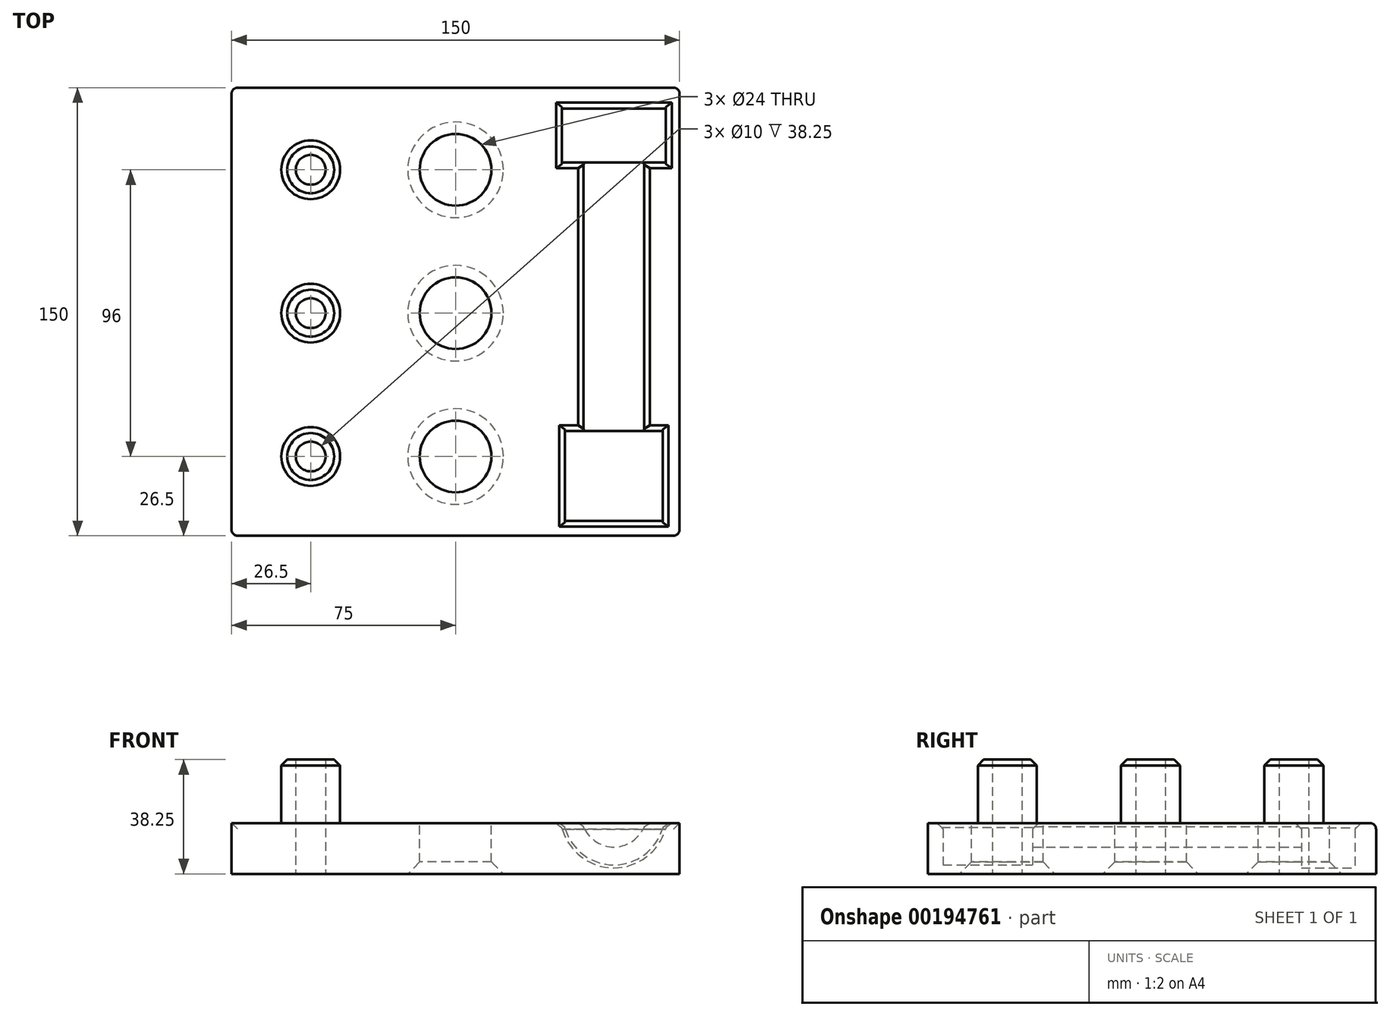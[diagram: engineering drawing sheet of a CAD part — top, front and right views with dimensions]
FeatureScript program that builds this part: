
annotation { "Feature Type Name" : "Feature", "Feature Type Description" : "" }
export const myFeature = defineFeature(function(context is Context, id is Id, definition is map)
    precondition{}
    {
        {
            var Q0;
            Q0=qCreatedBy(makeId("Top.planeOp"),FACE);
            var sketch = newSketch(context, id + "F0", { "sketchPlane" : qUnion([Q0])});
            skLineSegment(sketch, "E0.bottom", {"start": v(0, 0) * mm, "end": v(150, 0) * mm});
            skLineSegment(sketch, "E0.top", {"start": v(0, 150) * mm, "end": v(150, 150) * mm});
            skLineSegment(sketch, "E0.left", {"start": v(0, 0) * mm, "end": v(0, 150) * mm});
            skLineSegment(sketch, "E0.right", {"start": v(150, 0) * mm, "end": v(150, 150) * mm});
            skSolve(sketch);
        }
        {
            var Q0;
            Q0=makeQuery(id+"F0.imprint","IMPRINT",FACE,{"disambiguationData":[TD([[makeQuery(id+"F0.imprint","IMPRINT",EDGE,{"derivedFrom":sQuery(id+"F0.wireOp",EDGE,"E0.bottom")}),1.0]])]});
            extrude(context, id + "F1", {"entities" : qUnion([Q0]), "depth" : 20 * mm});
        }
        {
            var Q0;
            Q0=makeQuery(id+"F1.opExtrude","CAP_FACE",FACE,{"disambiguationData":[OSD([sQuery(id+"F0.wireOp",EDGE,"E0.bottom"),sQuery(id+"F0.wireOp",EDGE,"E0.top"),sQuery(id+"F0.wireOp",EDGE,"E0.left"),sQuery(id+"F0.wireOp",EDGE,"E0.right")])],"isStart":false});
            var sketch = newSketch(context, id + "F2", { "sketchPlane" : qUnion([Q0])});
            skLineSegment(sketch, "E1.bottom", {"start": v(150, 0) * mm, "end": v(128, 0) * mm, "construction": true});
            skLineSegment(sketch, "E1.top", {"start": v(150, 5) * mm, "end": v(128, 5) * mm, "construction": true});
            skLineSegment(sketch, "E1.left", {"start": v(150, 0) * mm, "end": v(150, 5) * mm, "construction": true});
            skLineSegment(sketch, "E1.right", {"start": v(128, 0) * mm, "end": v(128, 5) * mm, "construction": true});
            skLineSegment(sketch, "E2.bottom", {"start": v(128, 5) * mm, "end": v(111, 5) * mm});
            skLineSegment(sketch, "E2.top", {"start": v(117, 35) * mm, "end": v(111, 35) * mm});
            skLineSegment(sketch, "E2.left", {"start": v(128, 5) * mm, "end": v(128, 35) * mm});
            skLineSegment(sketch, "E2.right", {"start": v(111, 5) * mm, "end": v(111, 35) * mm});
            skLineSegment(sketch, "E3.left", {"start": v(128, 35) * mm, "end": v(128, 125) * mm});
            skLineSegment(sketch, "E3.right", {"start": v(117, 35) * mm, "end": v(117, 125) * mm});
            skLineSegment(sketch, "E4.bottom", {"start": v(117, 125) * mm, "end": v(110, 125) * mm});
            skLineSegment(sketch, "E4.top", {"start": v(128, 143) * mm, "end": v(110, 143) * mm});
            skLineSegment(sketch, "E4.left", {"start": v(128, 125) * mm, "end": v(128, 143) * mm});
            skLineSegment(sketch, "E4.right", {"start": v(110, 125) * mm, "end": v(110, 143) * mm});
            skSolve(sketch);
        }
        {
            var Q0;
            Q0=makeQuery(id+"F2.imprint","IMPRINT",FACE,{"disambiguationData":[TD([[makeQuery(id+"F2.imprint","IMPRINT",EDGE,{"derivedFrom":sQuery(id+"F2.wireOp",EDGE,"E2.bottom")}),-1.0]])]});
            var Q1;
            Q1=sQuery(id+"F2.wireOp",EDGE,"E3.left");
            revolve(context, id + "F3", {"operationType" : NewBodyOperationType.REMOVE, "entities" : qUnion([Q0]), "axis" : qUnion([Q1]), "revolveType" : RevolveType.FULL, "oppositeDirection" : true});
        }
        {
            var Q0;
            Q0=makeQuery(id+"F1.opExtrude","SWEPT_FACE",FACE,{"disambiguationData":[OSD([sQuery(id+"F0.wireOp",EDGE,"E0.bottom")])]});
            var sketch = newSketch(context, id + "F4", { "sketchPlane" : qUnion([Q0])});
            skLineSegment(sketch, "E5.bottom", {"start": v(0, 20) * mm, "end": v(150, 20) * mm});
            skLineSegment(sketch, "E5.top", {"start": v(0, 17) * mm, "end": v(150, 17) * mm});
            skLineSegment(sketch, "E5.left", {"start": v(0, 20) * mm, "end": v(0, 17) * mm});
            skLineSegment(sketch, "E5.right", {"start": v(150, 20) * mm, "end": v(150, 17) * mm});
            skSolve(sketch);
        }
        {
            var Q0;
            Q0=makeQuery(id+"F4.imprint","IMPRINT",FACE,{"disambiguationData":[TD([[makeQuery(id+"F4.imprint","IMPRINT",EDGE,{"derivedFrom":sQuery(id+"F4.wireOp",EDGE,"E5.bottom")}),-1.0]])]});
            extrude(context, id + "F5", {"entities" : qUnion([Q0]), "operationType" : NewBodyOperationType.REMOVE, "endBound" : BoundingType.THROUGH_ALL, "oppositeDirection" : true, "depth" : 25 * mm});
        }
        {
            var Q0;
            Q0=makeQuery(id+"F5.boolean.opBoolean","COPY",FACE,{"derivedFrom":makeQuery(id+"F5.opExtrude","SWEPT_FACE",FACE,{"disambiguationData":[OSD([sQuery(id+"F4.wireOp",EDGE,"E5.top")])]})});
            var sketch = newSketch(context, id + "F6", { "sketchPlane" : qUnion([Q0])});
            skLineSegment(sketch, "E6.bottom", {"start": v(0, 0) * mm, "end": v(75, 0) * mm, "construction": true});
            skLineSegment(sketch, "E6.top", {"start": v(0, 26.5) * mm, "end": v(75, 26.5) * mm, "construction": true});
            skLineSegment(sketch, "E6.left", {"start": v(0, 0) * mm, "end": v(0, 26.5) * mm, "construction": true});
            skLineSegment(sketch, "E6.right", {"start": v(75, 0) * mm, "end": v(75, 26.5) * mm, "construction": true});
            skLineSegment(sketch, "E7", {"start": v(75, 26.5) * mm, "end": v(75, 74.5) * mm, "construction": true});
            skLineSegment(sketch, "E8", {"start": v(75, 74.5) * mm, "end": v(75, 122.5) * mm, "construction": true});
            skPoint(sketch, "E8.endSnap0", {"position": v(75, 50.5) * mm});
            skCircle(sketch, "E9", {"center": v(75, 26.5) * mm, "radius": 12 * mm});
            skCircle(sketch, "E10", {"center": v(75, 74.5) * mm, "radius": 12 * mm});
            skCircle(sketch, "E11", {"center": v(75, 122.5) * mm, "radius": 12 * mm});
            skSolve(sketch);
        }
        {
            var Q0;
            Q0 = qSketchRegion(id + "F6", true);
            extrude(context, id + "F7", {"entities" : qUnion([Q0]), "operationType" : NewBodyOperationType.REMOVE, "endBound" : BoundingType.THROUGH_ALL, "oppositeDirection" : true, "depth" : 25 * mm});
        }
        {
            var Q0;
            Q0=makeQuery(id+"F5.boolean.opBoolean","COPY",FACE,{"derivedFrom":makeQuery(id+"F5.opExtrude","SWEPT_FACE",FACE,{"disambiguationData":[OSD([sQuery(id+"F4.wireOp",EDGE,"E5.top")])]})});
            var sketch = newSketch(context, id + "F8", { "sketchPlane" : qUnion([Q0])});
            skLineSegment(sketch, "E12.bottom", {"start": v(0, 0) * mm, "end": v(26.5, 0) * mm, "construction": true});
            skLineSegment(sketch, "E12.top", {"start": v(0, 26.5) * mm, "end": v(26.5, 26.5) * mm, "construction": true});
            skLineSegment(sketch, "E12.left", {"start": v(0, 0) * mm, "end": v(0, 26.5) * mm, "construction": true});
            skLineSegment(sketch, "E12.right", {"start": v(26.5, 0) * mm, "end": v(26.5, 26.5) * mm, "construction": true});
            skCircle(sketch, "E13", {"center": v(26.5, 26.5) * mm, "radius": 9.85 * mm});
            skLineSegment(sketch, "E14", {"start": v(26.5, 26.5) * mm, "end": v(26.5, 74.5) * mm, "construction": true});
            skLineSegment(sketch, "E15", {"start": v(26.5, 74.5) * mm, "end": v(26.5, 122.5) * mm, "construction": true});
            skPoint(sketch, "E15.endSnap0", {"position": v(26.5, 50.5) * mm});
            skCircle(sketch, "E16", {"center": v(26.5, 26.5) * mm, "radius": 5 * mm});
            skCircle(sketch, "E17", {"center": v(26.5, 74.5) * mm, "radius": 5 * mm});
            skCircle(sketch, "E18", {"center": v(26.5, 74.5) * mm, "radius": 9.85 * mm});
            skCircle(sketch, "E19", {"center": v(26.5, 122.5) * mm, "radius": 5 * mm});
            skCircle(sketch, "E20", {"center": v(26.5, 122.5) * mm, "radius": 9.85 * mm});
            skSolve(sketch);
        }
        {
            var Q0;
            Q0=makeQuery(id+"F8.imprint","IMPRINT",FACE,{"disambiguationData":[TD([[makeQuery(id+"F8.imprint","IMPRINT",EDGE,{"derivedFrom":sQuery(id+"F8.wireOp",EDGE,"E19")}),-1.0]])]});
            var Q1;
            Q1=makeQuery(id+"F8.imprint","IMPRINT",FACE,{"disambiguationData":[TD([[makeQuery(id+"F8.imprint","IMPRINT",EDGE,{"derivedFrom":sQuery(id+"F8.wireOp",EDGE,"E17")}),-1.0]])]});
            var Q2;
            Q2=makeQuery(id+"F8.imprint","IMPRINT",FACE,{"disambiguationData":[TD([[makeQuery(id+"F8.imprint","IMPRINT",EDGE,{"derivedFrom":sQuery(id+"F8.wireOp",EDGE,"E13")}),1.0]])]});
            extrude(context, id + "F9", {"entities" : qUnion([Q0, Q1, Q2]), "operationType" : NewBodyOperationType.ADD, "depth" : 21.25 * mm});
        }
        {
            var Q0;
            Q0=makeQuery(id+"F9.boolean.opBoolean","SPLIT",FACE,{"disambiguationData":[TD([makeQuery(id+"F9.opExtrude","SWEPT_FACE",FACE,{"disambiguationData":[OSD([sQuery(id+"F8.wireOp",EDGE,"E17")])]})])],"derivedFrom":makeQuery(id+"F5.boolean.opBoolean","COPY",FACE,{"derivedFrom":makeQuery(id+"F5.opExtrude","SWEPT_FACE",FACE,{"disambiguationData":[OSD([sQuery(id+"F4.wireOp",EDGE,"E5.top")])]})})});
            var Q1;
            Q1=makeQuery(id+"F9.boolean.opBoolean","SPLIT",FACE,{"disambiguationData":[TD([makeQuery(id+"F9.opExtrude","SWEPT_FACE",FACE,{"disambiguationData":[OSD([sQuery(id+"F8.wireOp",EDGE,"E19")])]})])],"derivedFrom":makeQuery(id+"F5.boolean.opBoolean","COPY",FACE,{"derivedFrom":makeQuery(id+"F5.opExtrude","SWEPT_FACE",FACE,{"disambiguationData":[OSD([sQuery(id+"F4.wireOp",EDGE,"E5.top")])]})})});
            var Q2;
            Q2=makeQuery(id+"F9.boolean.opBoolean","SPLIT",FACE,{"disambiguationData":[TD([makeQuery(id+"F9.opExtrude","SWEPT_FACE",FACE,{"disambiguationData":[OSD([sQuery(id+"F8.wireOp",EDGE,"E16")])]})])],"derivedFrom":makeQuery(id+"F5.boolean.opBoolean","COPY",FACE,{"derivedFrom":makeQuery(id+"F5.opExtrude","SWEPT_FACE",FACE,{"disambiguationData":[OSD([sQuery(id+"F4.wireOp",EDGE,"E5.top")])]})})});
            extrude(context, id + "F10", {"entities" : qUnion([Q0, Q1, Q2]), "operationType" : NewBodyOperationType.REMOVE, "endBound" : BoundingType.THROUGH_ALL, "oppositeDirection" : true, "depth" : 25 * mm});
        }
        {
            var Q0;
            Q0=makeQuery(id+"F9.opExtrude","CAP_EDGE",EDGE,{"disambiguationData":[OSD([sQuery(id+"F8.wireOp",EDGE,"E20")])],"isStart":false});
            var Q1;
            Q1=makeQuery(id+"F9.opExtrude","CAP_EDGE",EDGE,{"disambiguationData":[OSD([sQuery(id+"F8.wireOp",EDGE,"E18")])],"isStart":false});
            var Q2;
            Q2=makeQuery(id+"F9.opExtrude","CAP_EDGE",EDGE,{"disambiguationData":[OSD([sQuery(id+"F8.wireOp",EDGE,"E13")])],"isStart":false});
            var Q3;
            Q3=makeQuery(id+"F5.boolean.opBoolean","INTERSECT",EDGE,{"disambiguationData":[OD(0.0)],"derivedFrom":[makeQuery(id+"F3.boolean.opBoolean","COPY",FACE,{"derivedFrom":makeQuery(id+"F3.opRevolve","SWEPT_FACE",FACE,{"disambiguationData":[OSD([sQuery(id+"F2.wireOp",EDGE,"E3.right")])]})}),makeQuery(id+"F5.opExtrude","SWEPT_FACE",FACE,{"disambiguationData":[OSD([sQuery(id+"F4.wireOp",EDGE,"E5.top")])]})]});
            var Q4;
            Q4=makeQuery(id+"F5.boolean.opBoolean","INTERSECT",EDGE,{"disambiguationData":[OD(0.0)],"derivedFrom":[makeQuery(id+"F3.boolean.opBoolean","COPY",FACE,{"derivedFrom":makeQuery(id+"F3.opRevolve","SWEPT_FACE",FACE,{"disambiguationData":[OSD([sQuery(id+"F2.wireOp",EDGE,"E4.bottom")])]})}),makeQuery(id+"F5.opExtrude","SWEPT_FACE",FACE,{"disambiguationData":[OSD([sQuery(id+"F4.wireOp",EDGE,"E5.top")])]})]});
            var Q5;
            Q5=makeQuery(id+"F5.boolean.opBoolean","INTERSECT",EDGE,{"disambiguationData":[OD(0.0)],"derivedFrom":[makeQuery(id+"F3.boolean.opBoolean","COPY",FACE,{"derivedFrom":makeQuery(id+"F3.opRevolve","SWEPT_FACE",FACE,{"disambiguationData":[OSD([sQuery(id+"F2.wireOp",EDGE,"E4.right")])]})}),makeQuery(id+"F5.opExtrude","SWEPT_FACE",FACE,{"disambiguationData":[OSD([sQuery(id+"F4.wireOp",EDGE,"E5.top")])]})]});
            var Q6;
            Q6=makeQuery(id+"F5.boolean.opBoolean","INTERSECT",EDGE,{"derivedFrom":[makeQuery(id+"F3.boolean.opBoolean","COPY",FACE,{"derivedFrom":makeQuery(id+"F3.opRevolve","SWEPT_FACE",FACE,{"disambiguationData":[OSD([sQuery(id+"F2.wireOp",EDGE,"E4.top")])]})}),makeQuery(id+"F5.opExtrude","SWEPT_FACE",FACE,{"disambiguationData":[OSD([sQuery(id+"F4.wireOp",EDGE,"E5.top")])]})]});
            var Q7;
            Q7=makeQuery(id+"F5.boolean.opBoolean","INTERSECT",EDGE,{"disambiguationData":[OD(1.0)],"derivedFrom":[makeQuery(id+"F3.boolean.opBoolean","COPY",FACE,{"derivedFrom":makeQuery(id+"F3.opRevolve","SWEPT_FACE",FACE,{"disambiguationData":[OSD([sQuery(id+"F2.wireOp",EDGE,"E4.right")])]})}),makeQuery(id+"F5.opExtrude","SWEPT_FACE",FACE,{"disambiguationData":[OSD([sQuery(id+"F4.wireOp",EDGE,"E5.top")])]})]});
            var Q8;
            Q8=makeQuery(id+"F5.boolean.opBoolean","INTERSECT",EDGE,{"disambiguationData":[OD(1.0)],"derivedFrom":[makeQuery(id+"F3.boolean.opBoolean","COPY",FACE,{"derivedFrom":makeQuery(id+"F3.opRevolve","SWEPT_FACE",FACE,{"disambiguationData":[OSD([sQuery(id+"F2.wireOp",EDGE,"E4.bottom")])]})}),makeQuery(id+"F5.opExtrude","SWEPT_FACE",FACE,{"disambiguationData":[OSD([sQuery(id+"F4.wireOp",EDGE,"E5.top")])]})]});
            var Q9;
            Q9=makeQuery(id+"F5.boolean.opBoolean","INTERSECT",EDGE,{"disambiguationData":[OD(1.0)],"derivedFrom":[makeQuery(id+"F3.boolean.opBoolean","COPY",FACE,{"derivedFrom":makeQuery(id+"F3.opRevolve","SWEPT_FACE",FACE,{"disambiguationData":[OSD([sQuery(id+"F2.wireOp",EDGE,"E3.right")])]})}),makeQuery(id+"F5.opExtrude","SWEPT_FACE",FACE,{"disambiguationData":[OSD([sQuery(id+"F4.wireOp",EDGE,"E5.top")])]})]});
            var Q10;
            Q10=makeQuery(id+"F5.boolean.opBoolean","INTERSECT",EDGE,{"disambiguationData":[OD(1.0)],"derivedFrom":[makeQuery(id+"F3.boolean.opBoolean","COPY",FACE,{"derivedFrom":makeQuery(id+"F3.opRevolve","SWEPT_FACE",FACE,{"disambiguationData":[OSD([sQuery(id+"F2.wireOp",EDGE,"E2.top")])]})}),makeQuery(id+"F5.opExtrude","SWEPT_FACE",FACE,{"disambiguationData":[OSD([sQuery(id+"F4.wireOp",EDGE,"E5.top")])]})]});
            var Q11;
            Q11=makeQuery(id+"F5.boolean.opBoolean","INTERSECT",EDGE,{"disambiguationData":[OD(0.0)],"derivedFrom":[makeQuery(id+"F3.boolean.opBoolean","COPY",FACE,{"derivedFrom":makeQuery(id+"F3.opRevolve","SWEPT_FACE",FACE,{"disambiguationData":[OSD([sQuery(id+"F2.wireOp",EDGE,"E2.top")])]})}),makeQuery(id+"F5.opExtrude","SWEPT_FACE",FACE,{"disambiguationData":[OSD([sQuery(id+"F4.wireOp",EDGE,"E5.top")])]})]});
            var Q12;
            Q12=makeQuery(id+"F5.boolean.opBoolean","INTERSECT",EDGE,{"disambiguationData":[OD(0.0)],"derivedFrom":[makeQuery(id+"F3.boolean.opBoolean","COPY",FACE,{"derivedFrom":makeQuery(id+"F3.opRevolve","SWEPT_FACE",FACE,{"disambiguationData":[OSD([sQuery(id+"F2.wireOp",EDGE,"E2.right")])]})}),makeQuery(id+"F5.opExtrude","SWEPT_FACE",FACE,{"disambiguationData":[OSD([sQuery(id+"F4.wireOp",EDGE,"E5.top")])]})]});
            var Q13;
            Q13=makeQuery(id+"F5.boolean.opBoolean","INTERSECT",EDGE,{"derivedFrom":[makeQuery(id+"F3.boolean.opBoolean","COPY",FACE,{"derivedFrom":makeQuery(id+"F3.opRevolve","SWEPT_FACE",FACE,{"disambiguationData":[OSD([sQuery(id+"F2.wireOp",EDGE,"E2.bottom")])]})}),makeQuery(id+"F5.opExtrude","SWEPT_FACE",FACE,{"disambiguationData":[OSD([sQuery(id+"F4.wireOp",EDGE,"E5.top")])]})]});
            var Q14;
            Q14=makeQuery(id+"F5.boolean.opBoolean","INTERSECT",EDGE,{"disambiguationData":[OD(1.0)],"derivedFrom":[makeQuery(id+"F3.boolean.opBoolean","COPY",FACE,{"derivedFrom":makeQuery(id+"F3.opRevolve","SWEPT_FACE",FACE,{"disambiguationData":[OSD([sQuery(id+"F2.wireOp",EDGE,"E2.right")])]})}),makeQuery(id+"F5.opExtrude","SWEPT_FACE",FACE,{"disambiguationData":[OSD([sQuery(id+"F4.wireOp",EDGE,"E5.top")])]})]});
            chamfer(context, id + "F11", {"entities" : qUnion([Q0, Q1, Q2, Q3, Q4, Q5, Q6, Q7, Q8, Q9, Q10, Q11, Q12, Q13, Q14]), "width" : 2 * mm, "tangentPropagation" : true});
        }
        {
            var Q0;
            Q0=makeQuery(id+"F7.boolean.opBoolean","COPY",EDGE,{"derivedFrom":makeQuery(id+"F7.opExtrude","CAP_EDGE",EDGE,{"disambiguationData":[OSD([sQuery(id+"F6.wireOp",EDGE,"E11")])],"isStart":true})});
            var Q1;
            Q1=makeQuery(id+"F7.boolean.opBoolean","COPY",EDGE,{"derivedFrom":makeQuery(id+"F7.opExtrude","CAP_EDGE",EDGE,{"disambiguationData":[OSD([sQuery(id+"F6.wireOp",EDGE,"E10")])],"isStart":true})});
            var Q2;
            Q2=makeQuery(id+"F7.boolean.opBoolean","COPY",EDGE,{"derivedFrom":makeQuery(id+"F7.opExtrude","CAP_EDGE",EDGE,{"disambiguationData":[OSD([sQuery(id+"F6.wireOp",EDGE,"E9")])],"isStart":true})});
            var Q3;
            Q3=makeQuery(id+"F7.boolean.opBoolean","INTERSECT",EDGE,{"derivedFrom":[makeQuery(id+"F1.opExtrude","CAP_FACE",FACE,{"disambiguationData":[OSD([sQuery(id+"F0.wireOp",EDGE,"E0.bottom"),sQuery(id+"F0.wireOp",EDGE,"E0.top"),sQuery(id+"F0.wireOp",EDGE,"E0.left"),sQuery(id+"F0.wireOp",EDGE,"E0.right")])],"isStart":true}),makeQuery(id+"F7.opExtrude","SWEPT_FACE",FACE,{"disambiguationData":[OSD([sQuery(id+"F6.wireOp",EDGE,"E9")])]})]});
            var Q4;
            Q4=makeQuery(id+"F7.boolean.opBoolean","INTERSECT",EDGE,{"derivedFrom":[makeQuery(id+"F1.opExtrude","CAP_FACE",FACE,{"disambiguationData":[OSD([sQuery(id+"F0.wireOp",EDGE,"E0.bottom"),sQuery(id+"F0.wireOp",EDGE,"E0.top"),sQuery(id+"F0.wireOp",EDGE,"E0.left"),sQuery(id+"F0.wireOp",EDGE,"E0.right")])],"isStart":true}),makeQuery(id+"F7.opExtrude","SWEPT_FACE",FACE,{"disambiguationData":[OSD([sQuery(id+"F6.wireOp",EDGE,"E10")])]})]});
            var Q5;
            Q5=makeQuery(id+"F7.boolean.opBoolean","INTERSECT",EDGE,{"derivedFrom":[makeQuery(id+"F1.opExtrude","CAP_FACE",FACE,{"disambiguationData":[OSD([sQuery(id+"F0.wireOp",EDGE,"E0.bottom"),sQuery(id+"F0.wireOp",EDGE,"E0.top"),sQuery(id+"F0.wireOp",EDGE,"E0.left"),sQuery(id+"F0.wireOp",EDGE,"E0.right")])],"isStart":true}),makeQuery(id+"F7.opExtrude","SWEPT_FACE",FACE,{"disambiguationData":[OSD([sQuery(id+"F6.wireOp",EDGE,"E11")])]})]});
            chamfer(context, id + "F12", {"entities" : qUnion([Q0, Q1, Q2, Q3, Q4, Q5]), "width" : 4 * mm, "tangentPropagation" : true});
        }
        {
            var Q0;
            Q0=makeQuery(id+"F5.boolean.opBoolean","COPY",EDGE,{"derivedFrom":makeQuery(id+"F5.opExtrude","SWEPT_EDGE",EDGE,{"disambiguationData":[OSD([sQuery(id+"F0.wireOp",EDGE,"E0.bottom"),sQuery(id+"F0.wireOp",EDGE,"E0.left"),sQuery(id+"F4.wireOp",EDGE,"E5.top"),sQuery(id+"F4.wireOp",EDGE,"E5.left")])]})});
            var Q1;
            Q1=makeQuery(id+"F5.boolean.opBoolean","COPY",EDGE,{"derivedFrom":makeQuery(id+"F5.opExtrude","CAP_EDGE",EDGE,{"disambiguationData":[OSD([sQuery(id+"F4.wireOp",EDGE,"E5.top")])],"isStart":true})});
            var Q2;
            Q2=makeQuery(id+"F5.boolean.opBoolean","COPY",EDGE,{"derivedFrom":makeQuery(id+"F5.opExtrude","SWEPT_EDGE",EDGE,{"disambiguationData":[OSD([sQuery(id+"F0.wireOp",EDGE,"E0.bottom"),sQuery(id+"F0.wireOp",EDGE,"E0.right"),sQuery(id+"F4.wireOp",EDGE,"E5.top"),sQuery(id+"F4.wireOp",EDGE,"E5.right")])]})});
            var Q3;
            Q3=makeQuery(id+"F5.boolean.opBoolean","INTERSECT",EDGE,{"derivedFrom":[makeQuery(id+"F1.opExtrude","SWEPT_FACE",FACE,{"disambiguationData":[OSD([sQuery(id+"F0.wireOp",EDGE,"E0.top")])]}),makeQuery(id+"F5.opExtrude","SWEPT_FACE",FACE,{"disambiguationData":[OSD([sQuery(id+"F4.wireOp",EDGE,"E5.top")])]})]});
            var Q4;
            Q4=makeQuery(id+"F1.opExtrude","SWEPT_EDGE",EDGE,{"disambiguationData":[OSD([sQuery(id+"F0.wireOp",EDGE,"E0.top"),sQuery(id+"F0.wireOp",EDGE,"E0.right")])]});
            var Q5;
            Q5=makeQuery(id+"F1.opExtrude","SWEPT_EDGE",EDGE,{"disambiguationData":[OSD([sQuery(id+"F0.wireOp",EDGE,"E0.bottom"),sQuery(id+"F0.wireOp",EDGE,"E0.right")])]});
            var Q6;
            Q6=makeQuery(id+"F1.opExtrude","SWEPT_EDGE",EDGE,{"disambiguationData":[OSD([sQuery(id+"F0.wireOp",EDGE,"E0.bottom"),sQuery(id+"F0.wireOp",EDGE,"E0.left")])]});
            var Q7;
            Q7=makeQuery(id+"F1.opExtrude","SWEPT_EDGE",EDGE,{"disambiguationData":[OSD([sQuery(id+"F0.wireOp",EDGE,"E0.top"),sQuery(id+"F0.wireOp",EDGE,"E0.left")])]});
            fillet(context, id + "F13", {"entities" : qUnion([Q0, Q1, Q2, Q3, Q4, Q5, Q6, Q7]), "radius" : 2 * mm, "tangentPropagation" : true, "allowEdgeOverflow" : false});
        }
    });
